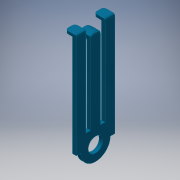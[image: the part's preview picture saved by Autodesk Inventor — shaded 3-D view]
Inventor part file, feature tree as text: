
AUTODESK INVENTOR PART (.ipt)
format: ipt  version: 2016 (Build 200138000, 138)  size: 396,800 bytes
history: native  units: in
note: dims shown in document units (in); Inventor stores cm internally (conversion verified against a paired STEP export)
features: extrude x14, sketch x14, reference x11, projected_geometry x9, fillet x8, plane x3
ambient origin geometry x8: Origin, YZ Plane, XZ Plane, XY Plane, X Axis, Y Axis, Z Axis, Center Point
bodies: Solid1 (feature_tree)
feature tree (59):
  extrude  "Extrusion1"  Depth=0.0079in
  sketch  "Sketch2"  dims[d12=0.052in d13=0.052in d14=0.052in]
  plane  "Work Plane1"
  plane  "Work Plane2"
  extrude  "Extrusion2"  Depth=0.052in
  fillet  "Fillet1"  Radius=0.052in
  extrude  "Extrusion3"  Depth=0.025in
  sketch  "Sketch4"  dims[d18=0.0197in d19=0.0in d20=0.0197in d21=0.0in]
  plane  "Work Plane3"
  extrude  "Extrusion4"  Depth=0.0197in TaperAngle=0.0deg
  extrude  "Extrusion5"  Depth=0.3937in TaperAngle=0.0deg
  fillet  "Fillet3"  Radius=0.0787in
  fillet  "Fillet4"  Radius=0.1969in
  extrude  "Extrusion6"  Depth=0.0394in
  fillet  "Fillet5"  Radius=0.1181in
  fillet  "Fillet6"  Radius=0.0394in
  extrude  "Extrusion7"  Depth=0.0157in
  fillet  "Fillet8"  Radius=0.052in
  extrude  "Extrusion8"  Depth=0.0039in
  fillet  "Fillet9"  Radius=0.0039in
  extrude  "Extrusion9"  Depth=0.0039in
  extrude  "Extrusion10"  Depth=1.0in TaperAngle=0.0deg
  extrude  "Extrusion11"  Depth=0.0079in TaperAngle=0.0deg
  extrude  "Extrusion12"  Depth=1.0in TaperAngle=0.0deg
  extrude  "Extrusion13"  Depth=0.0394in TaperAngle=0.0deg
  extrude  "Extrusion14"  Depth=0.0394in TaperAngle=0.0deg
  fillet  "Fillet11"  Radius=0.0157in
  sketch  "Sketch1"  dims[d9=0.0079in d11=0.0079in]
  reference  "Reference1"
  reference  "Reference2"
  reference  "Reference3"
  reference  "Reference4"
  reference  "Reference5"
  sketch  "Sketch3"  dims[d16=0.025in d17=0.025in]
  projected_geometry  "Projected Loop1"
  projected_geometry  "Projected Loop2"
  projected_geometry  "Projected Loop3"
  projected_geometry  "Projected Loop4"
  projected_geometry  "Projected Loop5"
  projected_geometry  "Projected Loop6"
  sketch  "Sketch5"  dims[d22=0.0197in d23=0.3937in d24=0.0in d25=0.0787in d26=0.1969in d27=0.0in]
  reference  "Reference6"
  reference  "Reference7"
  reference  "Reference8"
  sketch  "Sketch6"  dims[d29=0.0394in d30=0.0394in d31=0.1181in d32=0.0394in d33=0.0in]
  reference  "Reference9"
  sketch  "Sketch7"  dims[d34=0.0157in d35=0.0157in d36=0.052in]
  projected_geometry  "Projected Loop7"
  sketch  "Sketch8"  dims[d37=0.125in d38=0.0039in d39=0.0039in]
  sketch  "Sketch9"  dims[d40=1.0in d41=0.0in d42=0.0039in]
  sketch  "Sketch10"  dims[d43=0.0664in d45=1.0in d46=0.0in]
  sketch  "Sketch11"  dims[d47=0.0079in d48=1.0in d49=0.0in]
  projected_geometry  "Projected Loop8"
  sketch  "Sketch12"  dims[d50=0.4454in d51=1.0in d52=0.0in]
  reference  "Reference10"
  sketch  "Sketch13"  dims[d53=0.0394in d54=0.0in d55=0.0394in d56=0.0in]
  reference  "Reference11"
  sketch  "Sketch14"  dims[d58=0.0394in d59=0.0in d60=0.0394in d61=0.0in d62=0.0157in d63=0.0in d64=0.0079in]
  projected_geometry  "Projected Loop9"
